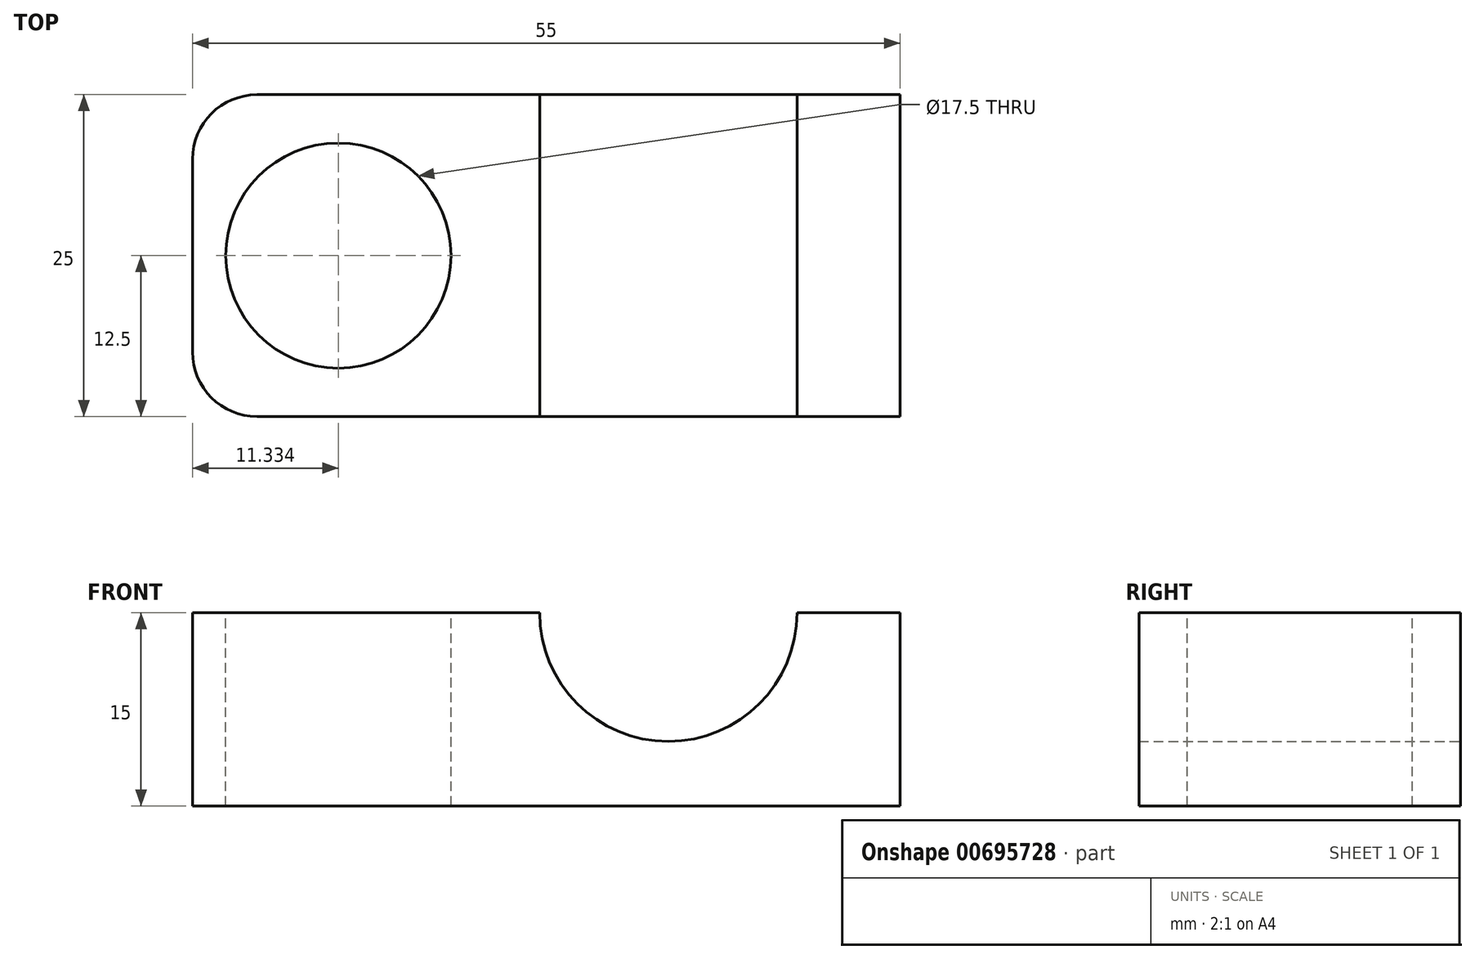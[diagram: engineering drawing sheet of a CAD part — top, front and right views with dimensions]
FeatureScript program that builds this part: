
annotation { "Feature Type Name" : "Feature", "Feature Type Description" : "" }
export const myFeature = defineFeature(function(context is Context, id is Id, definition is map)
    precondition{}
    {
        {
            var Q0;
            Q0=qCreatedBy(makeId("Front.planeOp"),FACE);
            var sketch = newSketch(context, id + "F0", { "sketchPlane" : qUnion([Q0])});
            skLineSegment(sketch, "E0.bottom", {"start": v(21.05, 0) * mm, "end": v(-33.95, 0) * mm});
            skLineSegment(sketch, "E0.top", {"start": v(21.05, 15) * mm, "end": v(13.03, 15) * mm});
            skLineSegment(sketch, "E0.left", {"start": v(21.05, 0) * mm, "end": v(21.05, 15) * mm});
            skLineSegment(sketch, "E0.right", {"start": v(-33.95, 0) * mm, "end": v(-33.95, 15) * mm});
            skArc(sketch, "E1", {"start": v(-6.97, 15) * mm, "mid": v(3.03, 5) * mm, "end": v(13.03, 15) * mm});
            skLineSegment(sketch, "E2.trimOffspring", {"start": v(-6.97, 15) * mm, "end": v(-33.95, 15) * mm});
            skSolve(sketch);
        }
        {
            var Q0;
            Q0 = qSketchRegion(id + "F0", true);
            extrude(context, id + "F1", {"entities" : qUnion([Q0]), "depth" : 25 * mm, "offsetDistance" : 25 * mm});
        }
        {
            var Q0;
            Q0=makeQuery(id+"F1.opExtrude","CAP_EDGE",EDGE,{"disambiguationData":[OSD([sQuery(id+"F0.wireOp",EDGE,"E0.right")])],"isStart":false});
            var Q1;
            Q1=makeQuery(id+"F1.opExtrude","CAP_EDGE",EDGE,{"disambiguationData":[OSD([sQuery(id+"F0.wireOp",EDGE,"E0.right")])],"isStart":true});
            fillet(context, id + "F2", {"entities" : qUnion([Q0, Q1]), "radius" : 5 * mm, "tangentPropagation" : true, "allowEdgeOverflow" : false});
        }
        {
            var Q0;
            Q0=makeQuery(id+"F1.opExtrude","SWEPT_FACE",FACE,{"disambiguationData":[OSD([sQuery(id+"F0.wireOp",EDGE,"E2.trimOffspring")])]});
            var sketch = newSketch(context, id + "F3", { "sketchPlane" : qUnion([Q0])});
            skPoint(sketch, "E3", {"position": v(-22.62, -12.5) * mm});
            skPoint(sketch, "E3.positionSnap0", {"position": v(-33.95, -12.5) * mm});
            skSolve(sketch);
        }
        {
            var Q0;
            Q0=sQuery(id+"F3.wireOp",VERTEX,"E3");
            var Q1;
            Q1=makeQuery(id+"F1.opExtrude","SWEPT_BODY",BODY,{"disambiguationData":[OSD([sQuery(id+"F0.wireOp",EDGE,"E0.bottom"),sQuery(id+"F0.wireOp",EDGE,"E0.top"),sQuery(id+"F0.wireOp",EDGE,"E0.left"),sQuery(id+"F0.wireOp",EDGE,"E0.right"),sQuery(id+"F0.wireOp",EDGE,"E1"),sQuery(id+"F0.wireOp",EDGE,"E2.trimOffspring")])]});
            hole(context, id + "F4", {"style" : HoleStyle.SIMPLE, "endStyle" : HoleEndStyle.THROUGH, "holeDiameter" : 17.5 * mm, "majorDiameter" : 5 * mm, "isTappedThrough" : true, "tappedDepth" : 12 * mm, "tapClearance" : 3, "locations" : qUnion([Q0]), "scope" : qUnion([Q1])});
        }
    });
